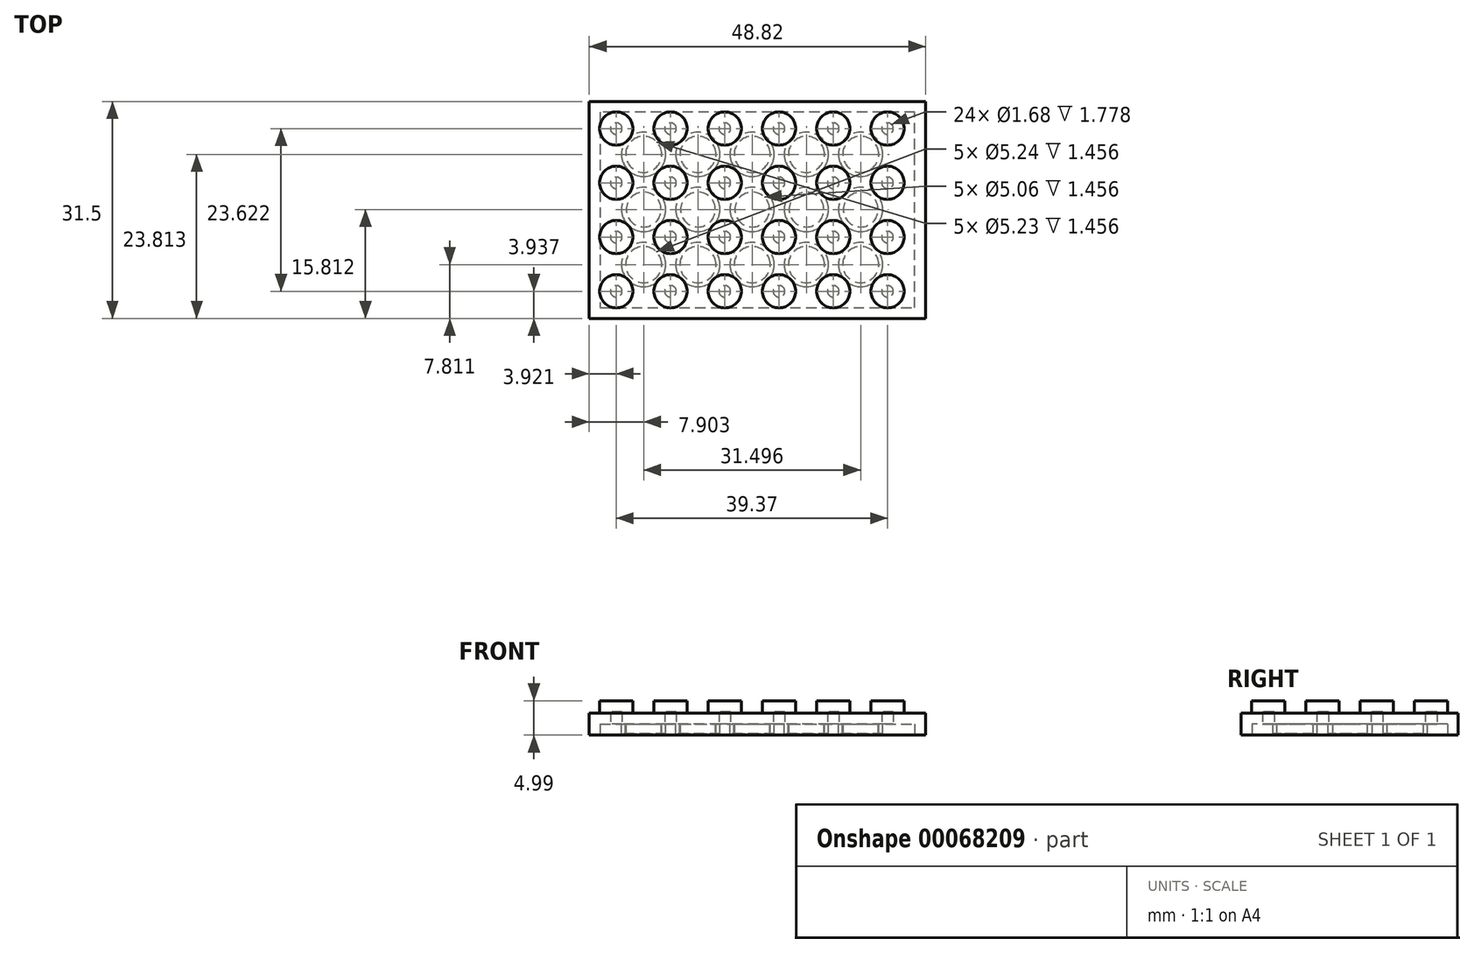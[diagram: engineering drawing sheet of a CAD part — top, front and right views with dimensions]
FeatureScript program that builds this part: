
annotation { "Feature Type Name" : "Feature", "Feature Type Description" : "" }
export const myFeature = defineFeature(function(context is Context, id is Id, definition is map)
    precondition{}
    {
        {
            var Q0;
            Q0=qCreatedBy(makeId("Top.planeOp"),FACE);
            var sketch = newSketch(context, id + "F0", { "sketchPlane" : qUnion([Q0])});
            skLineSegment(sketch, "E0", {"start": v(0, 0) * mm, "end": v(48.82, 0) * mm});
            skLineSegment(sketch, "E1", {"start": v(48.82, 0) * mm, "end": v(48.82, 31.5) * mm});
            skLineSegment(sketch, "E2", {"start": v(48.82, 31.5) * mm, "end": v(0, 31.5) * mm});
            skLineSegment(sketch, "E3", {"start": v(0, 31.5) * mm, "end": v(0, 0) * mm});
            skSolve(sketch);
        }
        {
            var Q0;
            Q0=makeQuery(id+"F0.imprint","IMPRINT",FACE,{"disambiguationData":[TD([[makeQuery(id+"F0.imprint","IMPRINT",EDGE,{"derivedFrom":sQuery(id+"F0.wireOp",EDGE,"E0")}),1.0]])]});
            extrude(context, id + "F1", {"entities" : qUnion([Q0]), "depth" : 3.2 * mm});
        }
        {
            var Q0;
            Q0=makeQuery(id+"F1.opExtrude","CAP_FACE",FACE,{"disambiguationData":[OSD([sQuery(id+"F0.wireOp",EDGE,"E0"),sQuery(id+"F0.wireOp",EDGE,"E1"),sQuery(id+"F0.wireOp",EDGE,"E2"),sQuery(id+"F0.wireOp",EDGE,"E3")])],"isStart":false});
            var sketch = newSketch(context, id + "F2", { "sketchPlane" : qUnion([Q0])});
            skCircle(sketch, "E4", {"center": v(3.92, 27.56) * mm, "radius": 2.41 * mm});
            skCircle(sketch, "E5", {"center": v(11.8, 27.56) * mm, "radius": 2.41 * mm});
            skCircle(sketch, "E6", {"center": v(19.67, 27.56) * mm, "radius": 2.41 * mm});
            skCircle(sketch, "E7", {"center": v(27.54, 27.56) * mm, "radius": 2.41 * mm});
            skCircle(sketch, "E8", {"center": v(35.42, 27.56) * mm, "radius": 2.41 * mm});
            skCircle(sketch, "E9", {"center": v(43.3, 27.56) * mm, "radius": 2.41 * mm});
            skCircle(sketch, "E10", {"center": v(3.92, 19.69) * mm, "radius": 2.41 * mm});
            skCircle(sketch, "E11", {"center": v(11.8, 19.69) * mm, "radius": 2.41 * mm});
            skCircle(sketch, "E12", {"center": v(19.67, 19.69) * mm, "radius": 2.41 * mm});
            skCircle(sketch, "E13", {"center": v(27.54, 19.69) * mm, "radius": 2.41 * mm});
            skCircle(sketch, "E14", {"center": v(35.42, 19.69) * mm, "radius": 2.41 * mm});
            skCircle(sketch, "E15", {"center": v(43.3, 19.69) * mm, "radius": 2.41 * mm});
            skCircle(sketch, "E16", {"center": v(3.92, 11.81) * mm, "radius": 2.41 * mm});
            skCircle(sketch, "E17", {"center": v(11.8, 11.81) * mm, "radius": 2.41 * mm});
            skCircle(sketch, "E18", {"center": v(19.67, 11.81) * mm, "radius": 2.41 * mm});
            skCircle(sketch, "E19", {"center": v(27.54, 11.81) * mm, "radius": 2.41 * mm});
            skCircle(sketch, "E20", {"center": v(35.42, 11.81) * mm, "radius": 2.41 * mm});
            skCircle(sketch, "E21", {"center": v(43.3, 11.81) * mm, "radius": 2.41 * mm});
            skCircle(sketch, "E22", {"center": v(3.92, 3.94) * mm, "radius": 2.41 * mm});
            skCircle(sketch, "E23", {"center": v(11.8, 3.94) * mm, "radius": 2.41 * mm});
            skCircle(sketch, "E24", {"center": v(19.67, 3.94) * mm, "radius": 2.41 * mm});
            skCircle(sketch, "E25", {"center": v(27.54, 3.94) * mm, "radius": 2.41 * mm});
            skCircle(sketch, "E26", {"center": v(35.42, 3.94) * mm, "radius": 2.41 * mm});
            skCircle(sketch, "E27", {"center": v(43.3, 3.94) * mm, "radius": 2.41 * mm});
            skSolve(sketch);
        }
        {
            var Q0;
            Q0=makeQuery(id+"F2.imprint","IMPRINT",FACE,{"disambiguationData":[TD([[makeQuery(id+"F2.imprint","IMPRINT",EDGE,{"derivedFrom":sQuery(id+"F2.wireOp",EDGE,"E4")}),1.0]])]});
            extrude(context, id + "F3", {"entities" : qUnion([Q0]), "operationType" : NewBodyOperationType.ADD, "depth" : 1.78 * mm});
        }
        {
            var Q0;
            Q0=makeQuery(id+"F2.imprint","IMPRINT",FACE,{"disambiguationData":[TD([[makeQuery(id+"F2.imprint","IMPRINT",EDGE,{"derivedFrom":sQuery(id+"F2.wireOp",EDGE,"E5")}),1.0]])]});
            extrude(context, id + "F4", {"entities" : qUnion([Q0]), "operationType" : NewBodyOperationType.ADD, "depth" : 1.78 * mm});
        }
        {
            var Q0;
            Q0=makeQuery(id+"F2.imprint","IMPRINT",FACE,{"disambiguationData":[TD([[makeQuery(id+"F2.imprint","IMPRINT",EDGE,{"derivedFrom":sQuery(id+"F2.wireOp",EDGE,"E6")}),1.0]])]});
            extrude(context, id + "F5", {"entities" : qUnion([Q0]), "operationType" : NewBodyOperationType.ADD, "depth" : 1.78 * mm});
        }
        {
            var Q0;
            Q0=makeQuery(id+"F2.imprint","IMPRINT",FACE,{"disambiguationData":[TD([[makeQuery(id+"F2.imprint","IMPRINT",EDGE,{"derivedFrom":sQuery(id+"F2.wireOp",EDGE,"E7")}),1.0]])]});
            extrude(context, id + "F6", {"entities" : qUnion([Q0]), "operationType" : NewBodyOperationType.ADD, "depth" : 1.78 * mm});
        }
        {
            var Q0;
            Q0=makeQuery(id+"F2.imprint","IMPRINT",FACE,{"disambiguationData":[TD([[makeQuery(id+"F2.imprint","IMPRINT",EDGE,{"derivedFrom":sQuery(id+"F2.wireOp",EDGE,"E8")}),1.0]])]});
            extrude(context, id + "F7", {"entities" : qUnion([Q0]), "operationType" : NewBodyOperationType.ADD, "depth" : 1.78 * mm});
        }
        {
            var Q0;
            Q0=makeQuery(id+"F2.imprint","IMPRINT",FACE,{"disambiguationData":[TD([[makeQuery(id+"F2.imprint","IMPRINT",EDGE,{"derivedFrom":sQuery(id+"F2.wireOp",EDGE,"E9")}),1.0]])]});
            var Q1;
            Q1=makeQuery(id+"F2.imprint","IMPRINT",FACE,{"disambiguationData":[TD([[makeQuery(id+"F2.imprint","IMPRINT",EDGE,{"derivedFrom":sQuery(id+"F2.wireOp",EDGE,"E10")}),1.0]])]});
            var Q2;
            Q2=makeQuery(id+"F2.imprint","IMPRINT",FACE,{"disambiguationData":[TD([[makeQuery(id+"F2.imprint","IMPRINT",EDGE,{"derivedFrom":sQuery(id+"F2.wireOp",EDGE,"E11")}),1.0]])]});
            var Q3;
            Q3=makeQuery(id+"F2.imprint","IMPRINT",FACE,{"disambiguationData":[TD([[makeQuery(id+"F2.imprint","IMPRINT",EDGE,{"derivedFrom":sQuery(id+"F2.wireOp",EDGE,"E12")}),1.0]])]});
            var Q4;
            Q4=makeQuery(id+"F2.imprint","IMPRINT",FACE,{"disambiguationData":[TD([[makeQuery(id+"F2.imprint","IMPRINT",EDGE,{"derivedFrom":sQuery(id+"F2.wireOp",EDGE,"E13")}),1.0]])]});
            var Q5;
            Q5=makeQuery(id+"F2.imprint","IMPRINT",FACE,{"disambiguationData":[TD([[makeQuery(id+"F2.imprint","IMPRINT",EDGE,{"derivedFrom":sQuery(id+"F2.wireOp",EDGE,"E14")}),1.0]])]});
            var Q6;
            Q6=makeQuery(id+"F2.imprint","IMPRINT",FACE,{"disambiguationData":[TD([[makeQuery(id+"F2.imprint","IMPRINT",EDGE,{"derivedFrom":sQuery(id+"F2.wireOp",EDGE,"E15")}),1.0]])]});
            var Q7;
            Q7=makeQuery(id+"F2.imprint","IMPRINT",FACE,{"disambiguationData":[TD([[makeQuery(id+"F2.imprint","IMPRINT",EDGE,{"derivedFrom":sQuery(id+"F2.wireOp",EDGE,"E21")}),1.0]])]});
            var Q8;
            Q8=makeQuery(id+"F2.imprint","IMPRINT",FACE,{"disambiguationData":[TD([[makeQuery(id+"F2.imprint","IMPRINT",EDGE,{"derivedFrom":sQuery(id+"F2.wireOp",EDGE,"E20")}),1.0]])]});
            var Q9;
            Q9=makeQuery(id+"F2.imprint","IMPRINT",FACE,{"disambiguationData":[TD([[makeQuery(id+"F2.imprint","IMPRINT",EDGE,{"derivedFrom":sQuery(id+"F2.wireOp",EDGE,"E19")}),1.0]])]});
            var Q10;
            Q10=makeQuery(id+"F2.imprint","IMPRINT",FACE,{"disambiguationData":[TD([[makeQuery(id+"F2.imprint","IMPRINT",EDGE,{"derivedFrom":sQuery(id+"F2.wireOp",EDGE,"E18")}),1.0]])]});
            var Q11;
            Q11=makeQuery(id+"F2.imprint","IMPRINT",FACE,{"disambiguationData":[TD([[makeQuery(id+"F2.imprint","IMPRINT",EDGE,{"derivedFrom":sQuery(id+"F2.wireOp",EDGE,"E17")}),1.0]])]});
            var Q12;
            Q12=makeQuery(id+"F2.imprint","IMPRINT",FACE,{"disambiguationData":[TD([[makeQuery(id+"F2.imprint","IMPRINT",EDGE,{"derivedFrom":sQuery(id+"F2.wireOp",EDGE,"E16")}),1.0]])]});
            var Q13;
            Q13=makeQuery(id+"F2.imprint","IMPRINT",FACE,{"disambiguationData":[TD([[makeQuery(id+"F2.imprint","IMPRINT",EDGE,{"derivedFrom":sQuery(id+"F2.wireOp",EDGE,"E22")}),1.0]])]});
            var Q14;
            Q14=makeQuery(id+"F2.imprint","IMPRINT",FACE,{"disambiguationData":[TD([[makeQuery(id+"F2.imprint","IMPRINT",EDGE,{"derivedFrom":sQuery(id+"F2.wireOp",EDGE,"E23")}),1.0]])]});
            var Q15;
            Q15=makeQuery(id+"F2.imprint","IMPRINT",FACE,{"disambiguationData":[TD([[makeQuery(id+"F2.imprint","IMPRINT",EDGE,{"derivedFrom":sQuery(id+"F2.wireOp",EDGE,"E24")}),1.0]])]});
            var Q16;
            Q16=makeQuery(id+"F2.imprint","IMPRINT",FACE,{"disambiguationData":[TD([[makeQuery(id+"F2.imprint","IMPRINT",EDGE,{"derivedFrom":sQuery(id+"F2.wireOp",EDGE,"E25")}),1.0]])]});
            var Q17;
            Q17=makeQuery(id+"F2.imprint","IMPRINT",FACE,{"disambiguationData":[TD([[makeQuery(id+"F2.imprint","IMPRINT",EDGE,{"derivedFrom":sQuery(id+"F2.wireOp",EDGE,"E26")}),1.0]])]});
            var Q18;
            Q18=makeQuery(id+"F2.imprint","IMPRINT",FACE,{"disambiguationData":[TD([[makeQuery(id+"F2.imprint","IMPRINT",EDGE,{"derivedFrom":sQuery(id+"F2.wireOp",EDGE,"E27")}),1.0]])]});
            extrude(context, id + "F8", {"entities" : qUnion([Q0, Q1, Q2, Q3, Q4, Q5, Q6, Q7, Q8, Q9, Q10, Q11, Q12, Q13, Q14, Q15, Q16, Q17, Q18]), "operationType" : NewBodyOperationType.ADD, "depth" : 1.78 * mm});
        }
        {
            var Q0;
            Q0=makeQuery(id+"F1.opExtrude","CAP_FACE",FACE,{"disambiguationData":[OSD([sQuery(id+"F0.wireOp",EDGE,"E0"),sQuery(id+"F0.wireOp",EDGE,"E1"),sQuery(id+"F0.wireOp",EDGE,"E2"),sQuery(id+"F0.wireOp",EDGE,"E3")])],"isStart":true});
            shell(context, id + "F9", {"entities" : qUnion([Q0]), "thickness" : 1.57 * mm});
        }
        {
            var Q0;
            Q0=makeQuery(id+"F9.opShell","OFFSET_FACE",FACE,{"disambiguationData":[OSD([sQuery(id+"F0.wireOp",EDGE,"E0"),sQuery(id+"F0.wireOp",EDGE,"E1"),sQuery(id+"F0.wireOp",EDGE,"E2"),sQuery(id+"F0.wireOp",EDGE,"E3")])]});
            var sketch = newSketch(context, id + "F10", { "sketchPlane" : qUnion([Q0])});
            skCircle(sketch, "E28", {"center": v(7.9, -7.81) * mm, "radius": 3.21 * mm});
            skCircle(sketch, "E29", {"center": v(7.9, -15.81) * mm, "radius": 3.21 * mm});
            skCircle(sketch, "E30", {"center": v(7.9, -23.81) * mm, "radius": 3.21 * mm});
            skCircle(sketch, "E31", {"center": v(7.9, -7.81) * mm, "radius": 2.62 * mm});
            skCircle(sketch, "E32", {"center": v(7.9, -15.81) * mm, "radius": 2.53 * mm});
            skCircle(sketch, "E33", {"center": v(7.9, -23.81) * mm, "radius": 2.61 * mm});
            skCircle(sketch, "E34.1.0.0", {"center": v(15.78, -7.81) * mm, "radius": 2.62 * mm});
            skCircle(sketch, "E34.1.0.1", {"center": v(15.78, -7.81) * mm, "radius": 3.21 * mm});
            skCircle(sketch, "E34.1.0.2", {"center": v(15.78, -15.81) * mm, "radius": 3.21 * mm});
            skCircle(sketch, "E34.1.0.3", {"center": v(15.78, -15.81) * mm, "radius": 2.53 * mm});
            skCircle(sketch, "E34.1.0.4", {"center": v(15.78, -23.81) * mm, "radius": 3.21 * mm});
            skCircle(sketch, "E34.1.0.5", {"center": v(15.78, -23.81) * mm, "radius": 2.61 * mm});
            skCircle(sketch, "E34.2.0.0", {"center": v(23.65, -7.81) * mm, "radius": 2.62 * mm});
            skCircle(sketch, "E34.2.0.1", {"center": v(23.65, -7.81) * mm, "radius": 3.21 * mm});
            skCircle(sketch, "E34.2.0.2", {"center": v(23.65, -15.81) * mm, "radius": 3.21 * mm});
            skCircle(sketch, "E34.2.0.3", {"center": v(23.65, -15.81) * mm, "radius": 2.53 * mm});
            skCircle(sketch, "E34.2.0.4", {"center": v(23.65, -23.81) * mm, "radius": 3.21 * mm});
            skCircle(sketch, "E34.2.0.5", {"center": v(23.65, -23.81) * mm, "radius": 2.61 * mm});
            skCircle(sketch, "E34.3.0.0", {"center": v(31.53, -7.81) * mm, "radius": 2.62 * mm});
            skCircle(sketch, "E34.3.0.1", {"center": v(31.53, -7.81) * mm, "radius": 3.21 * mm});
            skCircle(sketch, "E34.3.0.2", {"center": v(31.53, -15.81) * mm, "radius": 3.21 * mm});
            skCircle(sketch, "E34.3.0.3", {"center": v(31.53, -15.81) * mm, "radius": 2.53 * mm});
            skCircle(sketch, "E34.3.0.4", {"center": v(31.53, -23.81) * mm, "radius": 3.21 * mm});
            skCircle(sketch, "E34.3.0.5", {"center": v(31.53, -23.81) * mm, "radius": 2.61 * mm});
            skCircle(sketch, "E34.4.0.0", {"center": v(39.4, -7.81) * mm, "radius": 2.62 * mm});
            skCircle(sketch, "E34.4.0.1", {"center": v(39.4, -7.81) * mm, "radius": 3.21 * mm});
            skCircle(sketch, "E34.4.0.2", {"center": v(39.4, -15.81) * mm, "radius": 3.21 * mm});
            skCircle(sketch, "E34.4.0.3", {"center": v(39.4, -15.81) * mm, "radius": 2.53 * mm});
            skCircle(sketch, "E34.4.0.4", {"center": v(39.4, -23.81) * mm, "radius": 3.21 * mm});
            skCircle(sketch, "E34.4.0.5", {"center": v(39.4, -23.81) * mm, "radius": 2.61 * mm});
            skLineSegment(sketch, "E34.direction1", {"start": v(7.9, -7.81) * mm, "end": v(15.78, -7.81) * mm, "construction": true});
            skSolve(sketch);
        }
        {
            var Q0;
            Q0=makeQuery(id+"F10.imprint","IMPRINT",FACE,{"disambiguationData":[TD([[makeQuery(id+"F10.imprint","IMPRINT",EDGE,{"derivedFrom":sQuery(id+"F10.wireOp",EDGE,"E34.1.0.0")}),-1.0]])]});
            var Q1;
            Q1=makeQuery(id+"F10.imprint","IMPRINT",FACE,{"disambiguationData":[TD([[makeQuery(id+"F10.imprint","IMPRINT",EDGE,{"derivedFrom":sQuery(id+"F10.wireOp",EDGE,"E28")}),1.0]])]});
            var Q2;
            Q2=makeQuery(id+"F10.imprint","IMPRINT",FACE,{"disambiguationData":[TD([[makeQuery(id+"F10.imprint","IMPRINT",EDGE,{"derivedFrom":sQuery(id+"F10.wireOp",EDGE,"E34.2.0.0")}),-1.0]])]});
            var Q3;
            Q3=makeQuery(id+"F10.imprint","IMPRINT",FACE,{"disambiguationData":[TD([[makeQuery(id+"F10.imprint","IMPRINT",EDGE,{"derivedFrom":sQuery(id+"F10.wireOp",EDGE,"E34.3.0.0")}),-1.0]])]});
            var Q4;
            Q4=makeQuery(id+"F10.imprint","IMPRINT",FACE,{"disambiguationData":[TD([[makeQuery(id+"F10.imprint","IMPRINT",EDGE,{"derivedFrom":sQuery(id+"F10.wireOp",EDGE,"E34.4.0.0")}),-1.0]])]});
            var Q5;
            Q5=makeQuery(id+"F10.imprint","IMPRINT",FACE,{"disambiguationData":[TD([[makeQuery(id+"F10.imprint","IMPRINT",EDGE,{"derivedFrom":sQuery(id+"F10.wireOp",EDGE,"E34.4.0.2")}),1.0]])]});
            var Q6;
            Q6=makeQuery(id+"F10.imprint","IMPRINT",FACE,{"disambiguationData":[TD([[makeQuery(id+"F10.imprint","IMPRINT",EDGE,{"derivedFrom":sQuery(id+"F10.wireOp",EDGE,"E34.3.0.2")}),1.0]])]});
            var Q7;
            Q7=makeQuery(id+"F10.imprint","IMPRINT",FACE,{"disambiguationData":[TD([[makeQuery(id+"F10.imprint","IMPRINT",EDGE,{"derivedFrom":sQuery(id+"F10.wireOp",EDGE,"E34.2.0.2")}),1.0]])]});
            var Q8;
            Q8=makeQuery(id+"F10.imprint","IMPRINT",FACE,{"disambiguationData":[TD([[makeQuery(id+"F10.imprint","IMPRINT",EDGE,{"derivedFrom":sQuery(id+"F10.wireOp",EDGE,"E34.1.0.2")}),1.0]])]});
            var Q9;
            Q9=makeQuery(id+"F10.imprint","IMPRINT",FACE,{"disambiguationData":[TD([[makeQuery(id+"F10.imprint","IMPRINT",EDGE,{"derivedFrom":sQuery(id+"F10.wireOp",EDGE,"E29")}),1.0]])]});
            var Q10;
            Q10=makeQuery(id+"F10.imprint","IMPRINT",FACE,{"disambiguationData":[TD([[makeQuery(id+"F10.imprint","IMPRINT",EDGE,{"derivedFrom":sQuery(id+"F10.wireOp",EDGE,"E30")}),1.0]])]});
            var Q11;
            Q11=makeQuery(id+"F10.imprint","IMPRINT",FACE,{"disambiguationData":[TD([[makeQuery(id+"F10.imprint","IMPRINT",EDGE,{"derivedFrom":sQuery(id+"F10.wireOp",EDGE,"E34.1.0.4")}),1.0]])]});
            var Q12;
            Q12=makeQuery(id+"F10.imprint","IMPRINT",FACE,{"disambiguationData":[TD([[makeQuery(id+"F10.imprint","IMPRINT",EDGE,{"derivedFrom":sQuery(id+"F10.wireOp",EDGE,"E34.2.0.4")}),1.0]])]});
            var Q13;
            Q13=makeQuery(id+"F10.imprint","IMPRINT",FACE,{"disambiguationData":[TD([[makeQuery(id+"F10.imprint","IMPRINT",EDGE,{"derivedFrom":sQuery(id+"F10.wireOp",EDGE,"E34.3.0.4")}),1.0]])]});
            var Q14;
            Q14=makeQuery(id+"F10.imprint","IMPRINT",FACE,{"disambiguationData":[TD([[makeQuery(id+"F10.imprint","IMPRINT",EDGE,{"derivedFrom":sQuery(id+"F10.wireOp",EDGE,"E34.4.0.4")}),1.0]])]});
            extrude(context, id + "F11", {"entities" : qUnion([Q0, Q1, Q2, Q3, Q4, Q5, Q6, Q7, Q8, Q9, Q10, Q11, Q12, Q13, Q14]), "operationType" : NewBodyOperationType.ADD, "depth" : 1.46 * mm});
        }
    });
